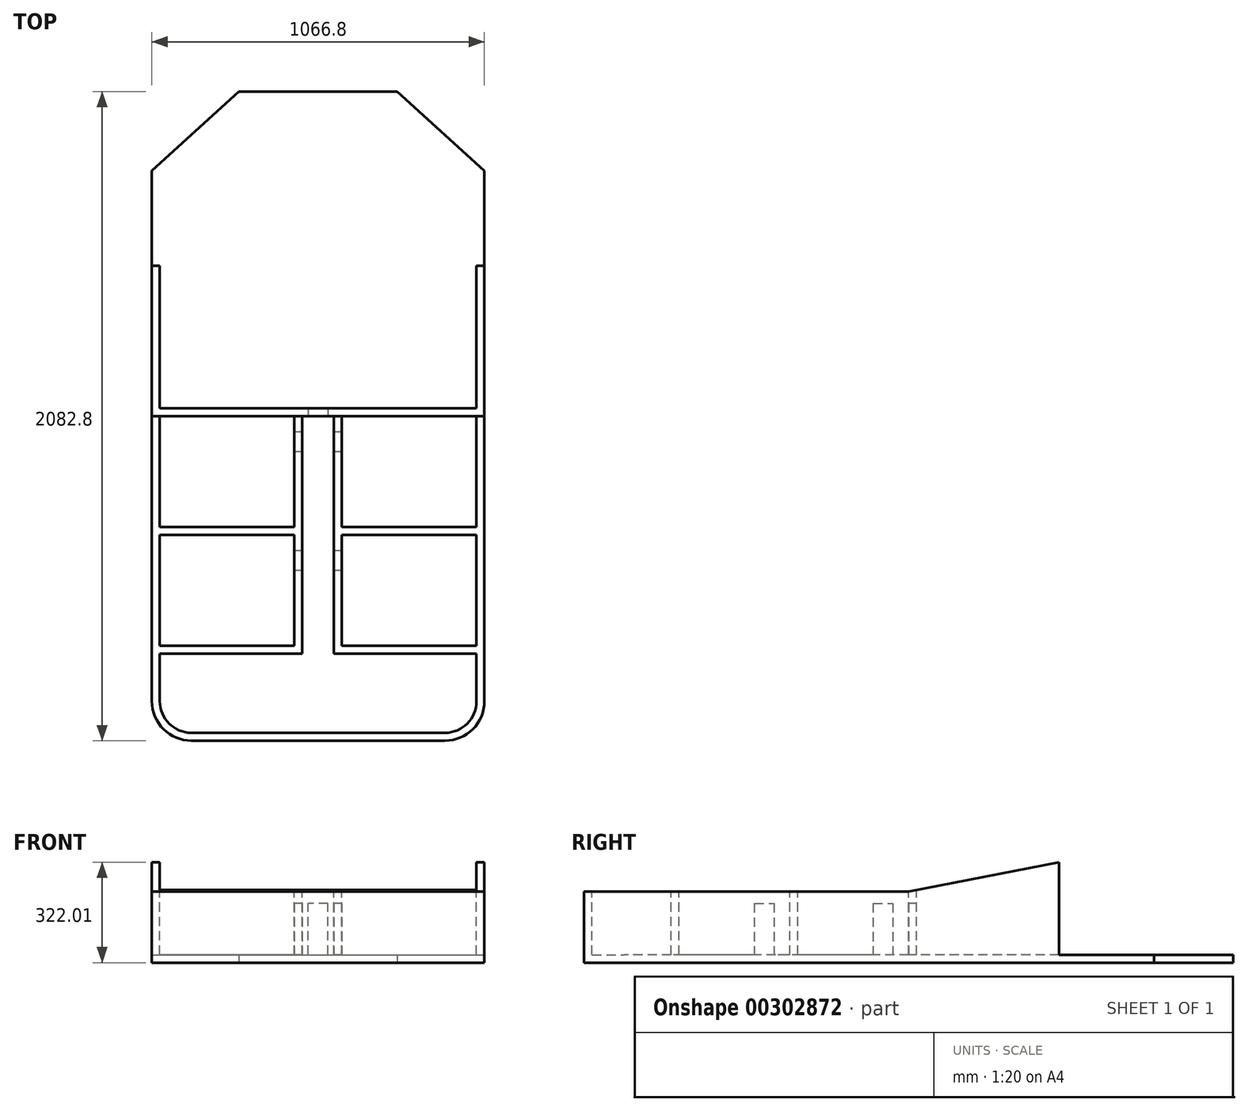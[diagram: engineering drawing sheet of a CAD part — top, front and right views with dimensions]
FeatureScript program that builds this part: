
annotation { "Feature Type Name" : "Feature", "Feature Type Description" : "" }
export const myFeature = defineFeature(function(context is Context, id is Id, definition is map)
    precondition{}
    {
        {
            var Q0;
            Q0=qCreatedBy(makeId("Top.planeOp"),FACE);
            var sketch = newSketch(context, id + "F0", { "sketchPlane" : qUnion([Q0])});
            skLineSegment(sketch, "E0.bottom", {"start": v(-533.4, 1041.4) * mm, "end": v(533.4, 1041.4) * mm});
            skLineSegment(sketch, "E0.top", {"start": v(-406.4, -1041.4) * mm, "end": v(406.4, -1041.4) * mm});
            skLineSegment(sketch, "E0.left", {"start": v(-533.4, 1041.4) * mm, "end": v(-533.4, -914.4) * mm});
            skLineSegment(sketch, "E0.right", {"start": v(533.4, 1041.4) * mm, "end": v(533.4, -914.4) * mm});
            skPoint(sketch, "E0.middle", {"position": v(0, 0) * mm});
            skPoint(sketch, "E1.visualSharp", {"position": v(-533.4, -1041.4) * mm});
            skArc(sketch, "E1.filletArc", {"start": v(-533.4, -914.4) * mm, "mid": v(-496.2, -1004.2) * mm, "end": v(-406.4, -1041.4) * mm});
            skPoint(sketch, "E2.visualSharp", {"position": v(533.4, -1041.4) * mm});
            skArc(sketch, "E2.filletArc", {"start": v(406.4, -1041.4) * mm, "mid": v(496.2, -1004.2) * mm, "end": v(533.4, -914.4) * mm});
            skLineSegment(sketch, "E3", {"start": v(-533.4, 787.4) * mm, "end": v(-254, 1041.4) * mm});
            skLineSegment(sketch, "E4", {"start": v(254, 1041.4) * mm, "end": v(533.4, 787.4) * mm});
            skSolve(sketch);
        }
        {
            var Q0;
            Q0=makeQuery(id+"F0.imprint","IMPRINT",FACE,{"disambiguationData":[TD([[makeQuery(id+"F0.imprint","IMPRINT",EDGE,{"derivedFrom":sQuery(id+"F0.wireOp",EDGE,"E0.top")}),1.0]])]});
            extrude(context, id + "F1", {"entities" : qUnion([Q0]), "depth" : 381 * mm});
        }
        {
            var Q0;
            Q0=qCreatedBy(makeId("Right.planeOp"),FACE);
            var sketch = newSketch(context, id + "F2", { "sketchPlane" : qUnion([Q0])});
            skLineSegment(sketch, "E5", {"start": v(-1041.4, 228.6) * mm, "end": v(0, 228.6) * mm});
            skLineSegment(sketch, "E6", {"start": v(0, 228.6) * mm, "end": v(787.4, 381) * mm});
            skLineSegment(sketch, "E7", {"start": v(787.4, 381) * mm, "end": v(1016, 381) * mm});
            skLineSegment(sketch, "E8", {"start": v(-1041.4, 228.6) * mm, "end": v(-1041.4, 381) * mm});
            skLineSegment(sketch, "E9", {"start": v(-1041.4, 381) * mm, "end": v(787.4, 381) * mm});
            skSolve(sketch);
        }
        {
            var Q0;
            Q0=makeQuery(id+"F1.opExtrude","CAP_FACE",FACE,{"disambiguationData":[OSD([sQuery(id+"F0.wireOp",EDGE,"E0.bottom"),sQuery(id+"F0.wireOp",EDGE,"E0.top"),sQuery(id+"F0.wireOp",EDGE,"E0.left"),sQuery(id+"F0.wireOp",EDGE,"E0.right"),sQuery(id+"F0.wireOp",EDGE,"E1.filletArc"),sQuery(id+"F0.wireOp",EDGE,"E2.filletArc"),sQuery(id+"F0.wireOp",EDGE,"E3"),sQuery(id+"F0.wireOp",EDGE,"E4")])],"isStart":false});
            var sketch = newSketch(context, id + "F3", { "sketchPlane" : qUnion([Q0])});
            skLineSegment(sketch, "E10.0", {"start": v(-508, 776.16) * mm, "end": v(-508, -914.4) * mm});
            skArc(sketch, "E10.1", {"start": v(-508, -914.4) * mm, "mid": v(-478.24, -986.24) * mm, "end": v(-406.4, -1016) * mm});
            skLineSegment(sketch, "E10.2", {"start": v(-508, 776.16) * mm, "end": v(-244.18, 1016) * mm});
            skLineSegment(sketch, "E10.3", {"start": v(-406.4, -1016) * mm, "end": v(406.4, -1016) * mm});
            skLineSegment(sketch, "E10.4", {"start": v(-244.18, 1016) * mm, "end": v(244.18, 1016) * mm});
            skLineSegment(sketch, "E10.5", {"start": v(244.18, 1016) * mm, "end": v(508, 776.16) * mm});
            skLineSegment(sketch, "E10.6", {"start": v(508, 776.16) * mm, "end": v(508, -914.4) * mm});
            skArc(sketch, "E10.7", {"start": v(406.4, -1016) * mm, "mid": v(478.24, -986.24) * mm, "end": v(508, -914.4) * mm});
            skLineSegment(sketch, "E11", {"start": v(-508, 0) * mm, "end": v(508, 0) * mm});
            skLineSegment(sketch, "E12", {"start": v(-508, 25.4) * mm, "end": v(508, 25.4) * mm});
            skLineSegment(sketch, "E13", {"start": v(-50.8, 0) * mm, "end": v(-50.8, -381) * mm});
            skLineSegment(sketch, "E14", {"start": v(-50.8, -381) * mm, "end": v(-508, -381) * mm});
            skLineSegment(sketch, "E15", {"start": v(50.8, 0) * mm, "end": v(50.8, -381) * mm});
            skLineSegment(sketch, "E16", {"start": v(50.8, -381) * mm, "end": v(508, -381) * mm});
            skLineSegment(sketch, "E17.0", {"start": v(-76.2, -355.6) * mm, "end": v(-508, -355.6) * mm});
            skLineSegment(sketch, "E17.1", {"start": v(-76.2, 0) * mm, "end": v(-76.2, -355.6) * mm});
            skLineSegment(sketch, "E18.0", {"start": v(76.2, -355.6) * mm, "end": v(508, -355.6) * mm});
            skLineSegment(sketch, "E18.1", {"start": v(76.2, 0) * mm, "end": v(76.2, -355.6) * mm});
            skLineSegment(sketch, "E19", {"start": v(-50.8, -381) * mm, "end": v(-50.8, -762) * mm});
            skLineSegment(sketch, "E20", {"start": v(-50.8, -762) * mm, "end": v(-508, -762) * mm});
            skLineSegment(sketch, "E21", {"start": v(50.8, -381) * mm, "end": v(50.8, -762) * mm});
            skLineSegment(sketch, "E22", {"start": v(50.8, -762) * mm, "end": v(508, -762) * mm});
            skLineSegment(sketch, "E23.0", {"start": v(-76.2, -736.6) * mm, "end": v(-508, -736.6) * mm});
            skLineSegment(sketch, "E23.1", {"start": v(-76.2, -381) * mm, "end": v(-76.2, -736.6) * mm});
            skLineSegment(sketch, "E24.0", {"start": v(76.2, -736.6) * mm, "end": v(508, -736.6) * mm});
            skLineSegment(sketch, "E24.1", {"start": v(76.2, -381) * mm, "end": v(76.2, -736.6) * mm});
            skLineSegment(sketch, "E25", {"start": v(-508, 508) * mm, "end": v(508, 508) * mm});
            skLineSegment(sketch, "E26", {"start": v(-508, 482.6) * mm, "end": v(508, 482.6) * mm});
            skSolve(sketch);
        }
        {
            var Q0;
            {var subQ0=sQuery(id+"F3.wireOp",EDGE,"E12");Q0=makeQuery(id+"F3.imprint","IMPRINT",FACE,{"disambiguationData":[TD([[makeQuery(id+"F3.imprint","IMPRINT",EDGE,{"derivedFrom":subQ0}),1.0]])]});}
            var Q1;
            {var subQ1=sQuery(id+"F3.wireOp",EDGE,"E10.2");Q1=makeQuery(id+"F3.imprint","IMPRINT",FACE,{"disambiguationData":[TD([[makeQuery(id+"F3.imprint","IMPRINT",EDGE,{"derivedFrom":subQ1}),-1.0]])]});}
            var Q2;
            {var subQ3=sQuery(id+"F3.wireOp",EDGE,"E17.0");Q2=makeQuery(id+"F3.imprint","IMPRINT",FACE,{"disambiguationData":[TD([[makeQuery(id+"F3.imprint","IMPRINT",EDGE,{"derivedFrom":subQ3}),-1.0]])]});}
            var Q3;
            {var subQ3=sQuery(id+"F3.wireOp",EDGE,"E18.0");Q3=makeQuery(id+"F3.imprint","IMPRINT",FACE,{"disambiguationData":[TD([[makeQuery(id+"F3.imprint","IMPRINT",EDGE,{"derivedFrom":subQ3}),1.0]])]});}
            var Q4;
            {var subQ3=sQuery(id+"F3.wireOp",EDGE,"E24.0");Q4=makeQuery(id+"F3.imprint","IMPRINT",FACE,{"disambiguationData":[TD([[makeQuery(id+"F3.imprint","IMPRINT",EDGE,{"derivedFrom":subQ3}),1.0]])]});}
            var Q5;
            {var subQ3=sQuery(id+"F3.wireOp",EDGE,"E23.0");Q5=makeQuery(id+"F3.imprint","IMPRINT",FACE,{"disambiguationData":[TD([[makeQuery(id+"F3.imprint","IMPRINT",EDGE,{"derivedFrom":subQ3}),-1.0]])]});}
            var Q6;
            {var subQ5=sQuery(id+"F3.wireOp",EDGE,"E10.1");Q6=makeQuery(id+"F3.imprint","IMPRINT",FACE,{"disambiguationData":[TD([[makeQuery(id+"F3.imprint","IMPRINT",EDGE,{"derivedFrom":subQ5}),1.0]])]});}
            extrude(context, id + "F4", {"entities" : qUnion([Q0, Q1, Q2, Q3, Q4, Q5, Q6]), "operationType" : NewBodyOperationType.REMOVE, "oppositeDirection" : true, "depth" : 355.6 * mm});
        }
        {
            var Q0;
            Q0 = qSketchRegion(id + "F2", true);
            extrude(context, id + "F5", {"entities" : qUnion([Q0]), "operationType" : NewBodyOperationType.REMOVE, "endBound" : BoundingType.SYMMETRIC, "oppositeDirection" : true, "depth" : 2540 * mm});
        }
        {
            var Q0;
            Q0=makeQuery(id+"F4.boolean.opBoolean","COPY",FACE,{"derivedFrom":makeQuery(id+"F4.opExtrude","SWEPT_FACE",FACE,{"disambiguationData":[OSD([sQuery(id+"F3.wireOp",EDGE,"E26")])]})});
            var sketch = newSketch(context, id + "F6", { "sketchPlane" : qUnion([Q0])});
            skLineSegment(sketch, "E27.bottom", {"start": v(-31.75, 190.5) * mm, "end": v(31.75, 190.5) * mm});
            skLineSegment(sketch, "E27.top", {"start": v(-31.75, 25.4) * mm, "end": v(31.75, 25.4) * mm});
            skLineSegment(sketch, "E27.left", {"start": v(-31.75, 190.5) * mm, "end": v(-31.75, 25.4) * mm});
            skLineSegment(sketch, "E27.right", {"start": v(31.75, 190.5) * mm, "end": v(31.75, 25.4) * mm});
            skPoint(sketch, "E27.middle", {"position": v(0, 107.95) * mm});
            skSolve(sketch);
        }
        {
            var Q0;
            Q0 = qSketchRegion(id + "F6", true);
            extrude(context, id + "F7", {"entities" : qUnion([Q0]), "operationType" : NewBodyOperationType.REMOVE, "endBound" : BoundingType.UP_TO_NEXT, "oppositeDirection" : true, "depth" : 25.4 * mm});
        }
        {
            var Q0;
            {var subQ0=sQuery(id+"F3.wireOp",EDGE,"E11");Q0=makeQuery(id+"F4.boolean.opBoolean","COPY",FACE,{"derivedFrom":makeQuery(id+"F4.opExtrude","SWEPT_FACE",FACE,{"disambiguationData":[OSD([subQ0]),TDD([makeQuery(id+"F3.imprint","IMPRINT",EDGE,{"disambiguationData":[TD([[makeQuery(id+"F3.imprint","INTERSECT",VERTEX,{"derivedFrom":[subQ0,sQuery(id+"F3.wireOp",EDGE,"E13")]}),-1.0]])],"derivedFrom":subQ0})])]})});}
            var sketch = newSketch(context, id + "F8", { "sketchPlane" : qUnion([Q0])});
            skLineSegment(sketch, "E28.bottom", {"start": v(-31.75, 190.5) * mm, "end": v(31.75, 190.5) * mm});
            skLineSegment(sketch, "E28.top", {"start": v(-31.75, 25.4) * mm, "end": v(31.75, 25.4) * mm});
            skLineSegment(sketch, "E28.left", {"start": v(-31.75, 190.5) * mm, "end": v(-31.75, 25.4) * mm});
            skLineSegment(sketch, "E28.right", {"start": v(31.75, 190.5) * mm, "end": v(31.75, 25.4) * mm});
            skPoint(sketch, "E28.middle", {"position": v(0, 107.95) * mm});
            skSolve(sketch);
        }
        {
            var Q0;
            Q0 = qSketchRegion(id + "F8", true);
            extrude(context, id + "F9", {"entities" : qUnion([Q0]), "operationType" : NewBodyOperationType.REMOVE, "endBound" : BoundingType.UP_TO_NEXT, "oppositeDirection" : true, "depth" : 25.4 * mm});
        }
        {
            var Q0;
            Q0=qCreatedBy(makeId("Right.planeOp"),FACE);
            var sketch = newSketch(context, id + "F10", { "sketchPlane" : qUnion([Q0])});
            skLineSegment(sketch, "E29.bottom", {"start": v(-114.3, 190.5) * mm, "end": v(-50.8, 190.5) * mm});
            skLineSegment(sketch, "E29.top", {"start": v(-114.3, 25.4) * mm, "end": v(-50.8, 25.4) * mm});
            skLineSegment(sketch, "E29.left", {"start": v(-114.3, 190.5) * mm, "end": v(-114.3, 25.4) * mm});
            skLineSegment(sketch, "E29.right", {"start": v(-50.8, 190.5) * mm, "end": v(-50.8, 25.4) * mm});
            skPoint(sketch, "E29.middle", {"position": v(-82.55, 107.95) * mm});
            skLineSegment(sketch, "E30.bottom", {"start": v(-495.3, 190.5) * mm, "end": v(-431.8, 190.5) * mm});
            skLineSegment(sketch, "E30.top", {"start": v(-495.3, 25.4) * mm, "end": v(-431.8, 25.4) * mm});
            skLineSegment(sketch, "E30.left", {"start": v(-495.3, 190.5) * mm, "end": v(-495.3, 25.4) * mm});
            skLineSegment(sketch, "E30.right", {"start": v(-431.8, 190.5) * mm, "end": v(-431.8, 25.4) * mm});
            skPoint(sketch, "E30.middle", {"position": v(-463.55, 107.95) * mm});
            skSolve(sketch);
        }
        {
            var Q0;
            Q0 = qSketchRegion(id + "F10", true);
            extrude(context, id + "F11", {"entities" : qUnion([Q0]), "operationType" : NewBodyOperationType.REMOVE, "endBound" : BoundingType.SYMMETRIC, "depth" : 254 * mm});
        }
        {
            var Q0;
            Q0=makeQuery(id+"F1.opExtrude","SWEPT_FACE",FACE,{"disambiguationData":[OSD([sQuery(id+"F0.wireOp",EDGE,"E0.bottom")])]});
            var sketch = newSketch(context, id + "F12", { "sketchPlane" : qUnion([Q0])});
            skLineSegment(sketch, "E31.bottom", {"start": v(63.5, 203.2) * mm, "end": v(-63.5, 203.2) * mm});
            skLineSegment(sketch, "E31.top", {"start": v(63.5, 25.4) * mm, "end": v(-63.5, 25.4) * mm});
            skLineSegment(sketch, "E31.left", {"start": v(63.5, 203.2) * mm, "end": v(63.5, 25.4) * mm});
            skLineSegment(sketch, "E31.right", {"start": v(-63.5, 203.2) * mm, "end": v(-63.5, 25.4) * mm});
            skPoint(sketch, "E31.middle", {"position": v(0, 114.3) * mm});
            skArc(sketch, "E32", {"start": v(63.5, 203.2) * mm, "mid": v(0, 266.7) * mm, "end": v(-63.5, 203.2) * mm});
            skSolve(sketch);
        }
        {
            var Q0;
            Q0 = qSketchRegion(id + "F12", true);
            extrude(context, id + "F13", {"entities" : qUnion([Q0]), "operationType" : NewBodyOperationType.REMOVE, "oppositeDirection" : true, "depth" : 25.4 * mm});
        }
        {
            var Q0;
            {var subQ0=sQuery(id+"F3.wireOp",EDGE,"E10.6");var subQ1=sQuery(id+"F3.wireOp",EDGE,"E10.0");var subQ2=sQuery(id+"F3.wireOp",EDGE,"E11");Q0=makeQuery(id+"F13.boolean.opBoolean","MERGE",FACE,{"derivedFrom":[makeQuery(id+"F11.boolean.opBoolean","MERGE",FACE,{"derivedFrom":[makeQuery(id+"F4.boolean.opBoolean","COPY",FACE,{"derivedFrom":makeQuery(id+"F4.opExtrude","CAP_FACE",FACE,{"disambiguationData":[OSD([subQ1,subQ2,sQuery(id+"F3.wireOp",EDGE,"E17.0"),sQuery(id+"F3.wireOp",EDGE,"E17.1")])],"isStart":false})}),makeQuery(id+"F4.boolean.opBoolean","COPY",FACE,{"derivedFrom":makeQuery(id+"F4.opExtrude","CAP_FACE",FACE,{"disambiguationData":[OSD([subQ1,sQuery(id+"F3.wireOp",EDGE,"E14"),sQuery(id+"F3.wireOp",EDGE,"E23.0"),sQuery(id+"F3.wireOp",EDGE,"E23.1")])],"isStart":false})}),makeQuery(id+"F4.boolean.opBoolean","COPY",FACE,{"derivedFrom":makeQuery(id+"F4.opExtrude","CAP_FACE",FACE,{"disambiguationData":[OSD([subQ0,subQ2,sQuery(id+"F3.wireOp",EDGE,"E18.0"),sQuery(id+"F3.wireOp",EDGE,"E18.1")])],"isStart":false})}),makeQuery(id+"F4.boolean.opBoolean","COPY",FACE,{"derivedFrom":makeQuery(id+"F4.opExtrude","CAP_FACE",FACE,{"disambiguationData":[OSD([subQ0,sQuery(id+"F3.wireOp",EDGE,"E16"),sQuery(id+"F3.wireOp",EDGE,"E24.0"),sQuery(id+"F3.wireOp",EDGE,"E24.1")])],"isStart":false})}),makeQuery(id+"F9.boolean.opBoolean","MERGE",FACE,{"derivedFrom":[makeQuery(id+"F4.boolean.opBoolean","COPY",FACE,{"derivedFrom":makeQuery(id+"F4.opExtrude","CAP_FACE",FACE,{"disambiguationData":[OSD([subQ1,sQuery(id+"F3.wireOp",EDGE,"E10.1"),sQuery(id+"F3.wireOp",EDGE,"E10.3"),subQ0,sQuery(id+"F3.wireOp",EDGE,"E10.7"),subQ2,sQuery(id+"F3.wireOp",EDGE,"E13"),sQuery(id+"F3.wireOp",EDGE,"E15"),sQuery(id+"F3.wireOp",EDGE,"E19"),sQuery(id+"F3.wireOp",EDGE,"E20"),sQuery(id+"F3.wireOp",EDGE,"E21"),sQuery(id+"F3.wireOp",EDGE,"E22")])],"isStart":false})}),makeQuery(id+"F7.boolean.opBoolean","MERGE",FACE,{"derivedFrom":[makeQuery(id+"F4.boolean.opBoolean","COPY",FACE,{"derivedFrom":makeQuery(id+"F4.opExtrude","CAP_FACE",FACE,{"disambiguationData":[OSD([subQ1,sQuery(id+"F3.wireOp",EDGE,"E10.2"),sQuery(id+"F3.wireOp",EDGE,"E10.4"),sQuery(id+"F3.wireOp",EDGE,"E10.5"),subQ0,sQuery(id+"F3.wireOp",EDGE,"E25")])],"isStart":false})}),makeQuery(id+"F4.boolean.opBoolean","COPY",FACE,{"derivedFrom":makeQuery(id+"F4.opExtrude","CAP_FACE",FACE,{"disambiguationData":[OSD([subQ1,subQ0,sQuery(id+"F3.wireOp",EDGE,"E12"),sQuery(id+"F3.wireOp",EDGE,"E26")])],"isStart":false})}),makeQuery(id+"F7.opExtrude","SWEPT_FACE",FACE,{"disambiguationData":[OSD([sQuery(id+"F6.wireOp",EDGE,"E27.top")])]})]}),makeQuery(id+"F9.opExtrude","SWEPT_FACE",FACE,{"disambiguationData":[OSD([sQuery(id+"F8.wireOp",EDGE,"E28.top")])]})]}),makeQuery(id+"F11.opExtrude","SWEPT_FACE",FACE,{"disambiguationData":[OSD([sQuery(id+"F10.wireOp",EDGE,"E29.top")])]}),makeQuery(id+"F11.opExtrude","SWEPT_FACE",FACE,{"disambiguationData":[OSD([sQuery(id+"F10.wireOp",EDGE,"E30.top")])]})]}),makeQuery(id+"F13.opExtrude","SWEPT_FACE",FACE,{"disambiguationData":[OSD([sQuery(id+"F12.wireOp",EDGE,"E31.top")])]})]});}
            var sketch = newSketch(context, id + "F14", { "sketchPlane" : qUnion([Q0])});
            skLineSegment(sketch, "E33.bottom", {"start": v(-746.94, 1076.5) * mm, "end": v(746.94, 1076.5) * mm});
            skLineSegment(sketch, "E33.top", {"start": v(-746.94, 482.6) * mm, "end": v(746.94, 482.6) * mm});
            skLineSegment(sketch, "E33.left", {"start": v(-746.94, 1076.5) * mm, "end": v(-746.94, 482.6) * mm});
            skLineSegment(sketch, "E33.right", {"start": v(746.94, 1076.5) * mm, "end": v(746.94, 482.6) * mm});
            skPoint(sketch, "E33.middle", {"position": v(0, 779.55) * mm});
            skSolve(sketch);
        }
        {
            var Q0;
            Q0 = qSketchRegion(id + "F14", true);
            extrude(context, id + "F15", {"entities" : qUnion([Q0]), "operationType" : NewBodyOperationType.REMOVE, "endBound" : BoundingType.THROUGH_ALL, "depth" : 25.4 * mm});
        }
    });
